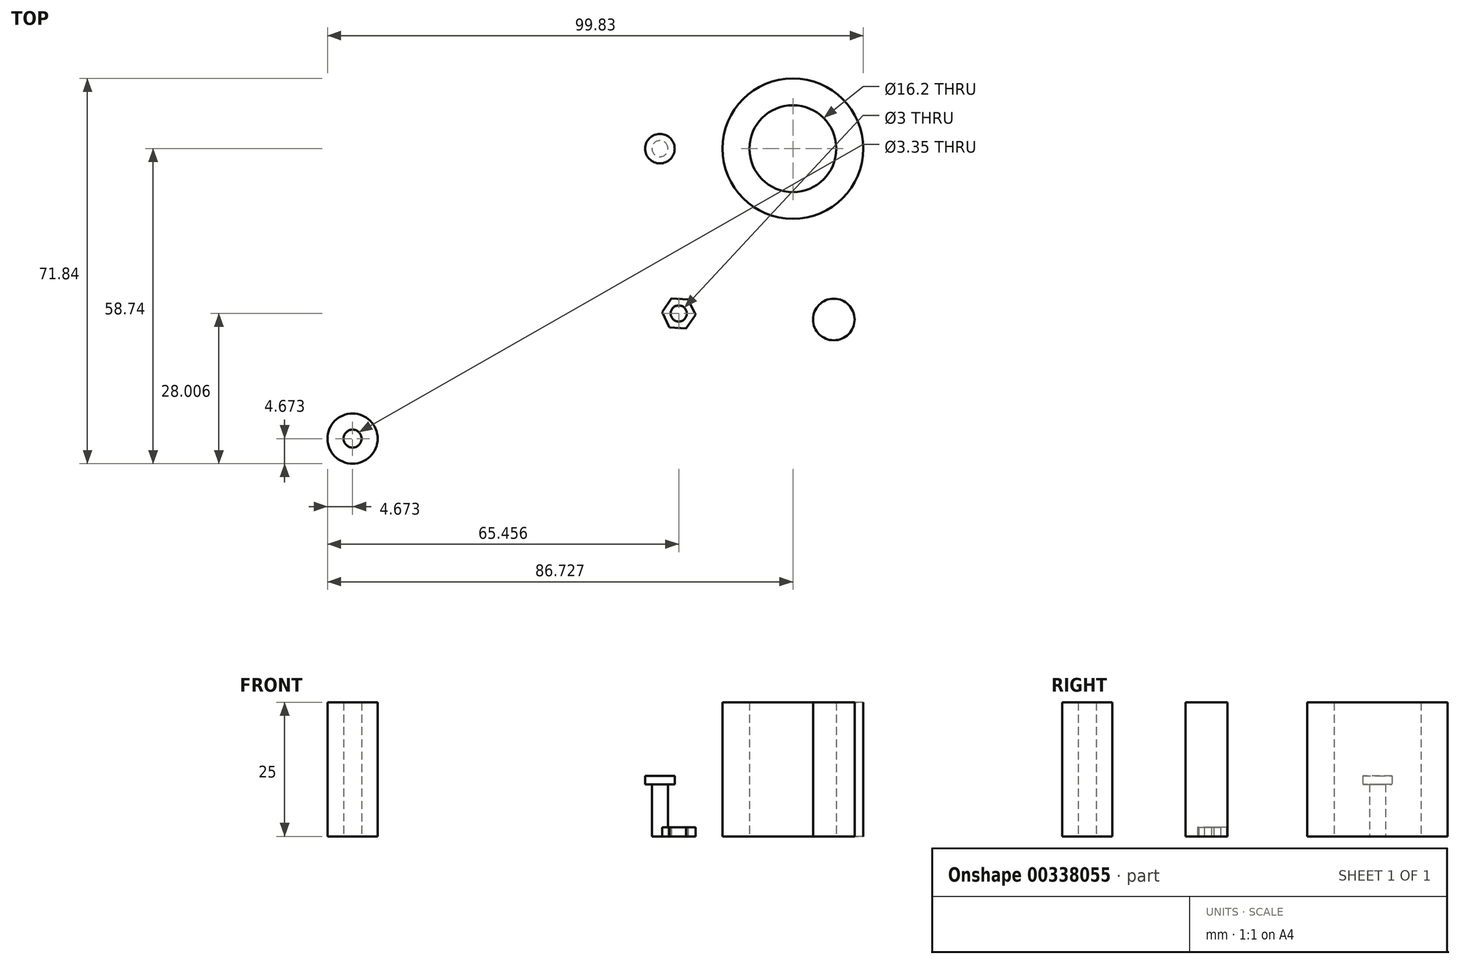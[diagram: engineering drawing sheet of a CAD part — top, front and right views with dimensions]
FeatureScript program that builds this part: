
annotation { "Feature Type Name" : "Feature", "Feature Type Description" : "" }
export const myFeature = defineFeature(function(context is Context, id is Id, definition is map)
    precondition{}
    {
        {
            var Q0;
            Q0=qCreatedBy(makeId("Top.planeOp"),FACE);
            var sketch = newSketch(context, id + "F0", { "sketchPlane" : qUnion([Q0])});
            skCircle(sketch, "E0", {"center": v(0, 0) * mm, "radius": 1.5 * mm});
            skSolve(sketch);
        }
        {
            var Q0;
            Q0=qSketchRegion(id+"F0",true);
            extrude(context, id + "F1", {"entities" : qUnion([Q0]), "depth" : 9.7 * mm});
        }
        {
            var Q0;
            Q0=makeQuery(id+"F1.opExtrude","CAP_FACE",FACE,{"disambiguationData":[OSD([sQuery(id+"F0.wireOp",EDGE,"E0")])],"isStart":false});
            var sketch = newSketch(context, id + "F2", { "sketchPlane" : qUnion([Q0])});
            skCircle(sketch, "E1", {"center": v(0, 0) * mm, "radius": 2.75 * mm});
            skSolve(sketch);
        }
        {
            var Q0;
            Q0=qSketchRegion(id+"F2",true);
            extrude(context, id + "F3", {"entities" : qUnion([Q0]), "operationType" : NewBodyOperationType.ADD, "depth" : 1.6 * mm});
        }
        {
            var Q0;
            Q0=qCreatedBy(makeId("Top.planeOp"),FACE);
            var sketch = newSketch(context, id + "F4", { "sketchPlane" : qUnion([Q0])});
            skCircle(sketch, "E2.cCircle", {"center": v(3.5, -30.73) * mm, "radius": 2.7 * mm, "construction": true});
            skLineSegment(sketch, "E2.0", {"start": v(6.62, -30.96) * mm, "end": v(4.86, -33.54) * mm});
            skLineSegment(sketch, "E2.1", {"start": v(4.86, -33.54) * mm, "end": v(1.75, -33.31) * mm});
            skLineSegment(sketch, "E2.2", {"start": v(1.75, -33.31) * mm, "end": v(0.4, -30.5) * mm});
            skLineSegment(sketch, "E2.3", {"start": v(0.4, -30.5) * mm, "end": v(2.15, -27.93) * mm});
            skLineSegment(sketch, "E2.4", {"start": v(2.15, -27.93) * mm, "end": v(5.26, -28.15) * mm});
            skLineSegment(sketch, "E2.5", {"start": v(5.26, -28.15) * mm, "end": v(6.62, -30.96) * mm});
            skPoint(sketch, "E2.0.midPoint", {"position": v(5.74, -32.25) * mm});
            skCircle(sketch, "E3", {"center": v(3.5, -30.73) * mm, "radius": 1.5 * mm});
            skSolve(sketch);
        }
        {
            var Q0;
            Q0=qSketchRegion(id+"F4",true);
            extrude(context, id + "F5", {"entities" : qUnion([Q0]), "depth" : 1.66 * mm});
        }
        {
            var Q0;
            Q0=qCreatedBy(makeId("Top.planeOp"),FACE);
            var sketch = newSketch(context, id + "F6", { "sketchPlane" : qUnion([Q0])});
            skCircle(sketch, "E4", {"center": v(24.78, 0) * mm, "radius": 8.1 * mm});
            skCircle(sketch, "E5.0", {"center": v(24.78, 0) * mm, "radius": 13.1 * mm});
            skSolve(sketch);
        }
        {
            var Q0;
            Q0=qSketchRegion(id+"F6",true);
            extrude(context, id + "F7", {"entities" : qUnion([Q0]), "depth" : 25 * mm});
        }
        {
            var Q0;
            Q0=qCreatedBy(makeId("Top.planeOp"),FACE);
            var sketch = newSketch(context, id + "F8", { "sketchPlane" : qUnion([Q0])});
            skCircle(sketch, "E6", {"center": v(32.4, -31.85) * mm, "radius": 3.88 * mm});
            skSolve(sketch);
        }
        {
            var Q0;
            Q0=qSketchRegion(id+"F8",true);
            extrude(context, id + "F9", {"entities" : qUnion([Q0]), "depth" : 25 * mm});
        }
        {
            var Q0;
            Q0=qCreatedBy(makeId("Top.planeOp"),FACE);
            var sketch = newSketch(context, id + "F10", { "sketchPlane" : qUnion([Q0])});
            skCircle(sketch, "E7", {"center": v(-57.28, -54.07) * mm, "radius": 1.68 * mm});
            skCircle(sketch, "E8.0", {"center": v(-57.28, -54.07) * mm, "radius": 4.68 * mm});
            skSolve(sketch);
        }
        {
            var Q0;
            Q0=qSketchRegion(id+"F10",true);
            extrude(context, id + "F11", {"entities" : qUnion([Q0]), "depth" : 25 * mm});
        }
    });
